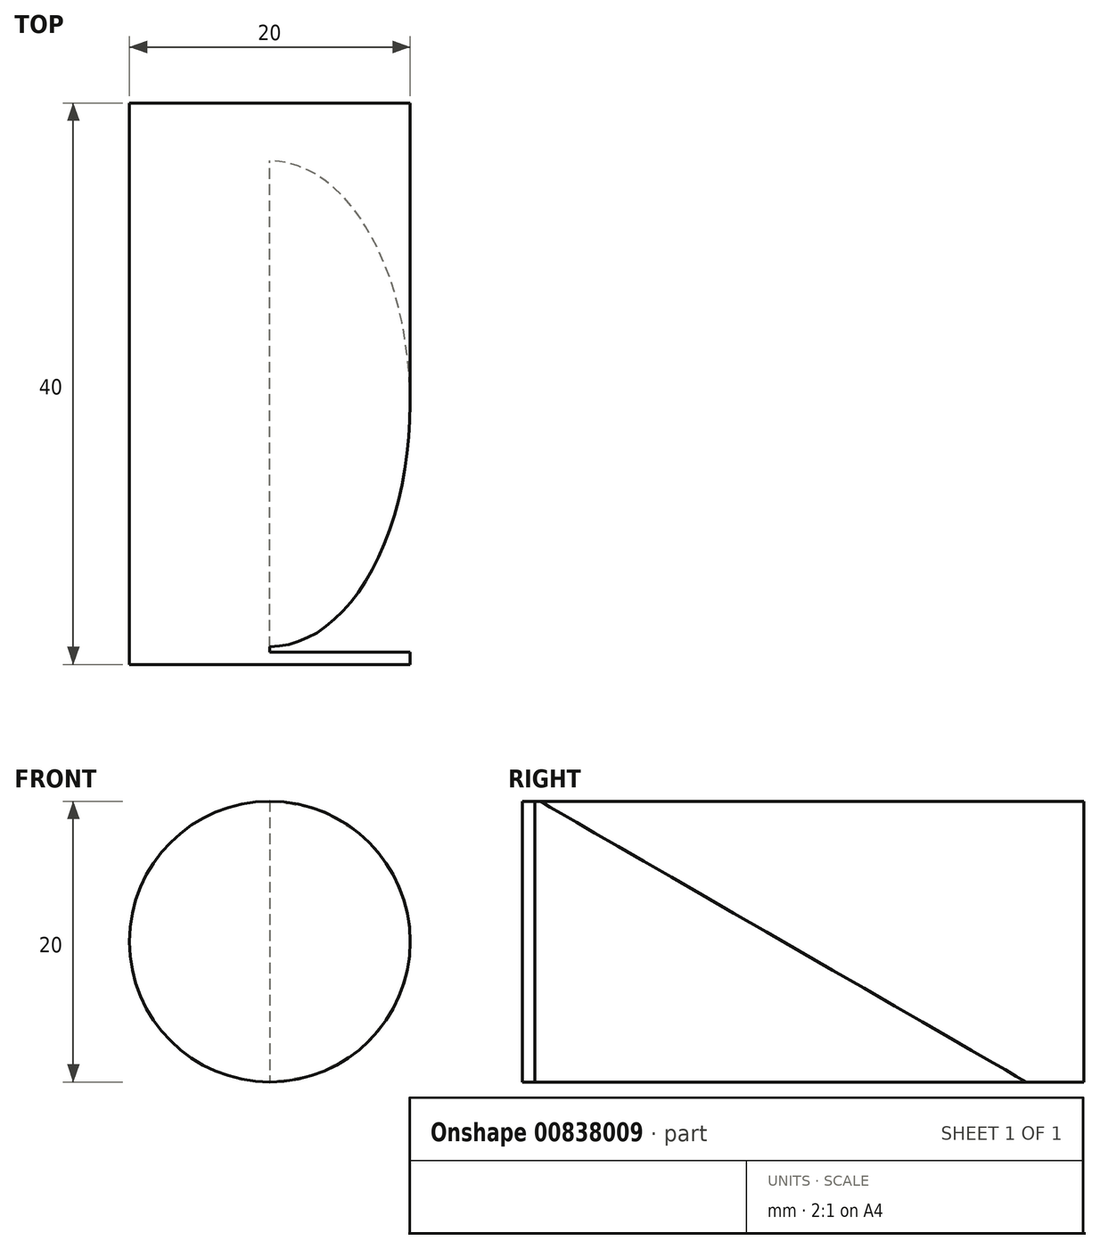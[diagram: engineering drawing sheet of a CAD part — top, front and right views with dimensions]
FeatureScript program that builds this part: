
annotation { "Feature Type Name" : "Feature", "Feature Type Description" : "" }
export const myFeature = defineFeature(function(context is Context, id is Id, definition is map)
    precondition{}
    {
        {
            var Q0;
            Q0=qCreatedBy(makeId("Front.planeOp"),FACE);
            var sketch = newSketch(context, id + "F0", { "sketchPlane" : qUnion([Q0])});
            skCircle(sketch, "E0", {"center": v(0, 0) * mm, "radius": 10 * mm});
            skSolve(sketch);
        }
        {
            var Q0;
            Q0=makeQuery(id+"F0.imprint","IMPRINT",FACE,{"disambiguationData":[TD([[makeQuery(id+"F0.imprint","IMPRINT",EDGE,{"derivedFrom":sQuery(id+"F0.wireOp",EDGE,"E0")}),1.0]])]});
            extrude(context, id + "F1", {"entities" : qUnion([Q0]), "depth" : 40 * mm, "offsetDistance" : 25 * mm});
        }
        {
            var Q0;
            Q0=makeQuery(id+"F1.opExtrude","CAP_FACE",FACE,{"disambiguationData":[OSD([sQuery(id+"F0.wireOp",EDGE,"E0")])],"isStart":false});
            var sketch = newSketch(context, id + "F2", { "sketchPlane" : qUnion([Q0])});
            skLineSegment(sketch, "E1", {"start": v(-17.8, 0) * mm, "end": v(16.77, 0) * mm});
            skSolve(sketch);
        }
        {
            var Q0;
            Q0=qCreatedBy(makeId("Right.planeOp"),FACE);
            var sketch = newSketch(context, id + "F3", { "sketchPlane" : qUnion([Q0])});
            skLineSegment(sketch, "E2", {"start": v(-116.4, 34.74) * mm, "end": v(-96.58, 0) * mm});
            skLineSegment(sketch, "E3", {"start": v(-39.13, 10.22) * mm, "end": v(-3.34, -10.45) * mm});
            skLineSegment(sketch, "E4", {"start": v(-39.13, 14.97) * mm, "end": v(-39.13, -15.08) * mm});
            skLineSegment(sketch, "E5", {"start": v(-3.34, -10.45) * mm, "end": v(-45.4, -10.45) * mm});
            skSolve(sketch);
        }
        {
            var Q0;
            Q0=qSketchRegion(id+"F3",true);
            extrude(context, id + "F4", {"entities" : qUnion([Q0]), "operationType" : NewBodyOperationType.REMOVE, "depth" : 80 * mm, "offsetDistance" : 25 * mm});
        }
    });
